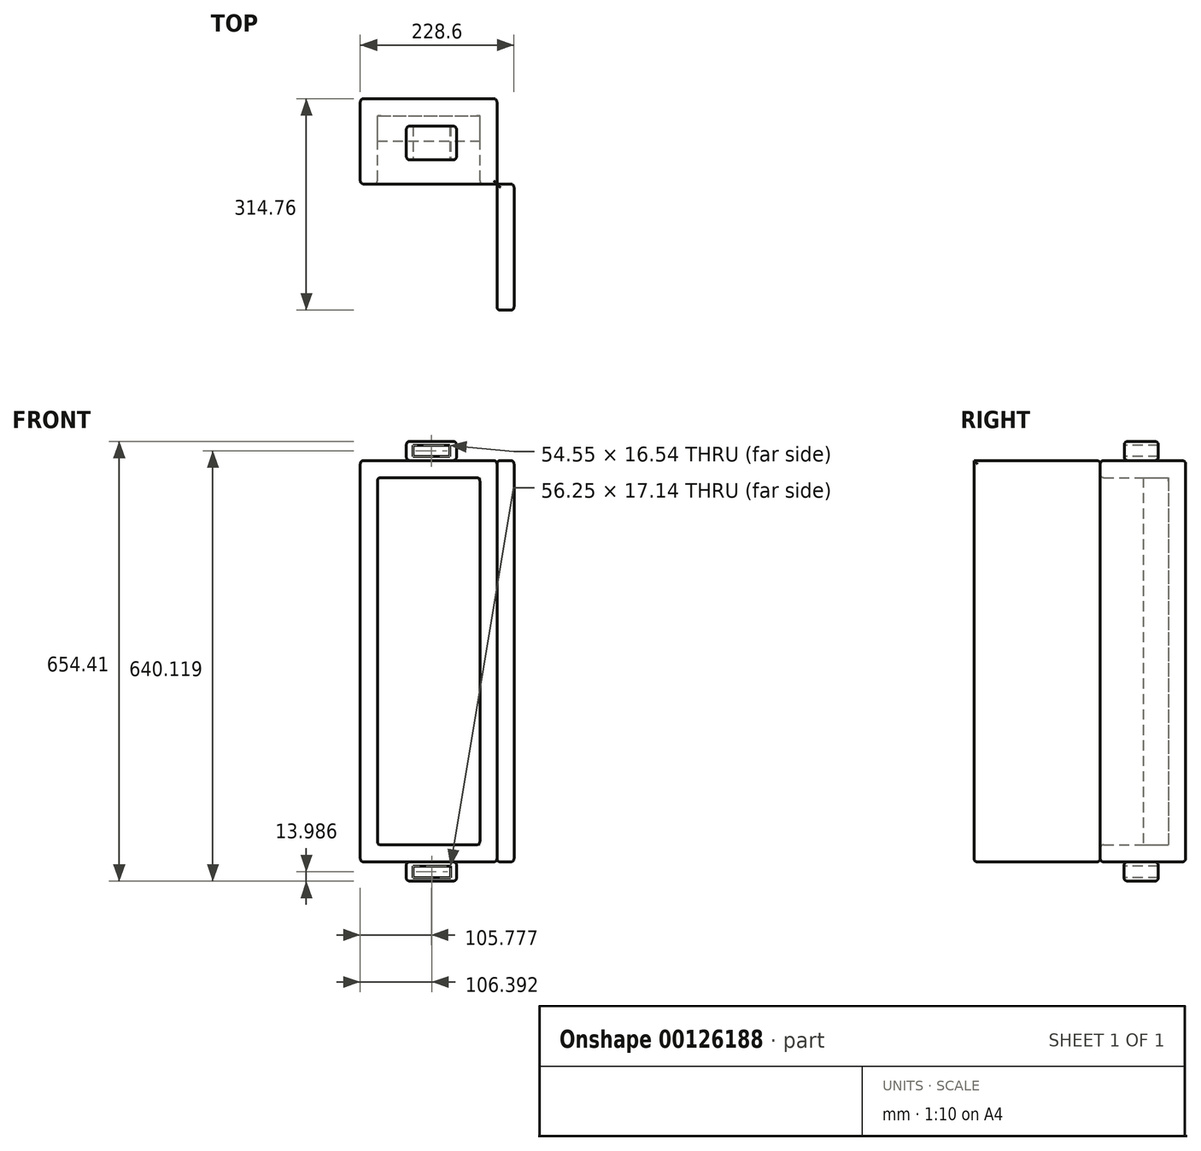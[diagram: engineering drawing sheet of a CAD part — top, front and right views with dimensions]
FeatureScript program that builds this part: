
annotation { "Feature Type Name" : "Feature", "Feature Type Description" : "" }
export const myFeature = defineFeature(function(context is Context, id is Id, definition is map)
    precondition{}
    {
        {
            var Q0;
            Q0=qCreatedBy(makeId("Front.planeOp"),FACE);
            var sketch = newSketch(context, id + "F0", { "sketchPlane" : qUnion([Q0])});
            skLineSegment(sketch, "E0.bottom", {"start": v(-31.04, 96) * mm, "end": v(172.16, 96) * mm});
            skLineSegment(sketch, "E0.top", {"start": v(-31.04, -501.25) * mm, "end": v(172.16, -501.25) * mm});
            skLineSegment(sketch, "E0.left", {"start": v(-31.04, 96) * mm, "end": v(-31.04, -501.25) * mm});
            skLineSegment(sketch, "E0.right", {"start": v(172.16, 96) * mm, "end": v(172.16, -501.25) * mm});
            skSolve(sketch);
        }
        {
            var Q0;
            Q0 = qSketchRegion(id + "F0", true);
            extrude(context, id + "F1", {"entities" : qUnion([Q0]), "depth" : 127 * mm});
        }
        {
            var Q0;
            Q0=makeQuery(id+"F1.opExtrude","CAP_FACE",FACE,{"disambiguationData":[OSD([sQuery(id+"F0.wireOp",EDGE,"E0.bottom"),sQuery(id+"F0.wireOp",EDGE,"E0.top"),sQuery(id+"F0.wireOp",EDGE,"E0.left"),sQuery(id+"F0.wireOp",EDGE,"E0.right")])],"isStart":false});
            shell(context, id + "F2", {"entities" : qUnion([Q0]), "thickness" : 25.4 * mm});
        }
        {
            var Q0;
            Q0=makeQuery(id+"F2.opShell","OFFSET_FACE",FACE,{"disambiguationData":[OSD([sQuery(id+"F0.wireOp",EDGE,"E0.bottom"),sQuery(id+"F0.wireOp",EDGE,"E0.top"),sQuery(id+"F0.wireOp",EDGE,"E0.left"),sQuery(id+"F0.wireOp",EDGE,"E0.right")])]});
            var sketch = newSketch(context, id + "F3", { "sketchPlane" : qUnion([Q0])});
            skLineSegment(sketch, "E1", {"start": v(-5.64, 70.6) * mm, "end": v(146.76, 70.6) * mm});
            skLineSegment(sketch, "E2", {"start": v(146.76, 70.6) * mm, "end": v(146.76, -475.85) * mm});
            skLineSegment(sketch, "E3", {"start": v(146.76, -475.85) * mm, "end": v(-5.64, -475.85) * mm});
            skLineSegment(sketch, "E4", {"start": v(-5.64, -475.85) * mm, "end": v(-5.64, 70.6) * mm});
            skSolve(sketch);
        }
        {
            var Q0;
            Q0 = qSketchRegion(id + "F3", true);
            extrude(context, id + "F4", {"entities" : qUnion([Q0]), "depth" : 37.53 * mm});
        }
        {
            var Q0;
            Q0=makeQuery(id+"F1.opExtrude","SWEPT_FACE",FACE,{"disambiguationData":[OSD([sQuery(id+"F0.wireOp",EDGE,"E0.right")])]});
            var sketch = newSketch(context, id + "F5", { "sketchPlane" : qUnion([Q0])});
            skLineSegment(sketch, "E5", {"start": v(-127, -501.25) * mm, "end": v(-314.76, -501.25) * mm});
            skLineSegment(sketch, "E6", {"start": v(-314.76, -501.25) * mm, "end": v(-314.76, 96) * mm});
            skLineSegment(sketch, "E7", {"start": v(-314.76, 96) * mm, "end": v(-127, 96) * mm});
            skLineSegment(sketch, "E8", {"start": v(-127, 96) * mm, "end": v(-127, -501.25) * mm});
            skSolve(sketch);
        }
        {
            var Q0;
            Q0 = qSketchRegion(id + "F5", true);
            extrude(context, id + "F6", {"entities" : qUnion([Q0]), "depth" : 25.4 * mm});
        }
        {
            var Q0;
            Q0=makeQuery(id+"F1.opExtrude","SWEPT_FACE",FACE,{"disambiguationData":[OSD([sQuery(id+"F0.wireOp",EDGE,"E0.top")])]});
            var sketch = newSketch(context, id + "F7", { "sketchPlane" : qUnion([Q0])});
            skLineSegment(sketch, "E9.bottom", {"start": v(37.26, 91.6) * mm, "end": v(112.22, 91.6) * mm});
            skLineSegment(sketch, "E9.top", {"start": v(37.26, 40.74) * mm, "end": v(112.22, 40.74) * mm});
            skLineSegment(sketch, "E9.left", {"start": v(37.26, 91.6) * mm, "end": v(37.26, 40.74) * mm});
            skLineSegment(sketch, "E9.right", {"start": v(112.22, 91.6) * mm, "end": v(112.22, 40.74) * mm});
            skSolve(sketch);
        }
        {
            var Q0;
            Q0 = qSketchRegion(id + "F7", true);
            extrude(context, id + "F8", {"entities" : qUnion([Q0]), "depth" : 28.58 * mm});
        }
        {
            var Q0;
            Q0=makeQuery(id+"F8.opExtrude","SWEPT_FACE",FACE,{"disambiguationData":[OSD([sQuery(id+"F7.wireOp",EDGE,"E9.bottom")])]});
            var sketch = newSketch(context, id + "F9", { "sketchPlane" : qUnion([Q0])});
            skLineSegment(sketch, "E10.bottom", {"start": v(47.23, -507.27) * mm, "end": v(103.48, -507.27) * mm});
            skLineSegment(sketch, "E10.top", {"start": v(47.23, -524.42) * mm, "end": v(103.48, -524.42) * mm});
            skLineSegment(sketch, "E10.left", {"start": v(47.23, -507.27) * mm, "end": v(47.23, -524.42) * mm});
            skLineSegment(sketch, "E10.right", {"start": v(103.48, -507.27) * mm, "end": v(103.48, -524.42) * mm});
            skSolve(sketch);
        }
        {
            var Q0;
            Q0 = qSketchRegion(id + "F9", true);
            extrude(context, id + "F10", {"entities" : qUnion([Q0]), "operationType" : NewBodyOperationType.REMOVE, "oppositeDirection" : true, "depth" : 76.2 * mm});
        }
        {
            var Q0;
            Q0=makeQuery(id+"F1.opExtrude","SWEPT_FACE",FACE,{"disambiguationData":[OSD([sQuery(id+"F0.wireOp",EDGE,"E0.bottom")])]});
            var sketch = newSketch(context, id + "F11", { "sketchPlane" : qUnion([Q0])});
            skLineSegment(sketch, "E11.bottom", {"start": v(37.48, -40.74) * mm, "end": v(112, -40.74) * mm});
            skLineSegment(sketch, "E11.top", {"start": v(37.48, -91.16) * mm, "end": v(112, -91.16) * mm});
            skLineSegment(sketch, "E11.left", {"start": v(37.48, -40.74) * mm, "end": v(37.48, -91.16) * mm});
            skLineSegment(sketch, "E11.right", {"start": v(112, -40.74) * mm, "end": v(112, -91.16) * mm});
            skSolve(sketch);
        }
        {
            var Q0;
            Q0 = qSketchRegion(id + "F11", true);
            extrude(context, id + "F12", {"entities" : qUnion([Q0]), "depth" : 28.57 * mm});
        }
        {
            var Q0;
            Q0=makeQuery(id+"F12.opExtrude","SWEPT_FACE",FACE,{"disambiguationData":[OSD([sQuery(id+"F11.wireOp",EDGE,"E11.top")])]});
            var sketch = newSketch(context, id + "F13", { "sketchPlane" : qUnion([Q0])});
            skLineSegment(sketch, "E12.bottom", {"start": v(47.46, 118.56) * mm, "end": v(102.01, 118.56) * mm});
            skLineSegment(sketch, "E12.top", {"start": v(47.46, 102.02) * mm, "end": v(102.01, 102.02) * mm});
            skLineSegment(sketch, "E12.left", {"start": v(47.46, 118.56) * mm, "end": v(47.46, 102.02) * mm});
            skLineSegment(sketch, "E12.right", {"start": v(102.01, 118.56) * mm, "end": v(102.01, 102.02) * mm});
            skSolve(sketch);
        }
        {
            var Q0;
            Q0 = qSketchRegion(id + "F13", true);
            extrude(context, id + "F14", {"entities" : qUnion([Q0]), "operationType" : NewBodyOperationType.REMOVE, "oppositeDirection" : true, "depth" : 76.2 * mm});
        }
        {
            var Q0;
            Q0=makeQuery(id+"F8.opExtrude","CAP_EDGE",EDGE,{"disambiguationData":[OSD([sQuery(id+"F7.wireOp",EDGE,"E9.left")])],"isStart":true});
            var Q1;
            Q1=makeQuery(id+"F8.opExtrude","CAP_EDGE",EDGE,{"disambiguationData":[OSD([sQuery(id+"F7.wireOp",EDGE,"E9.bottom")])],"isStart":true});
            var Q2;
            Q2=makeQuery(id+"F8.opExtrude","CAP_EDGE",EDGE,{"disambiguationData":[OSD([sQuery(id+"F7.wireOp",EDGE,"E9.right")])],"isStart":true});
            var Q3;
            Q3=makeQuery(id+"F8.opExtrude","CAP_EDGE",EDGE,{"disambiguationData":[OSD([sQuery(id+"F7.wireOp",EDGE,"E9.top")])],"isStart":true});
            var Q4;
            Q4=makeQuery(id+"F8.opExtrude","SWEPT_EDGE",EDGE,{"disambiguationData":[OSD([sQuery(id+"F7.wireOp",EDGE,"E9.top"),sQuery(id+"F7.wireOp",EDGE,"E9.right")])]});
            var Q5;
            Q5=makeQuery(id+"F8.opExtrude","SWEPT_EDGE",EDGE,{"disambiguationData":[OSD([sQuery(id+"F7.wireOp",EDGE,"E9.bottom"),sQuery(id+"F7.wireOp",EDGE,"E9.right")])]});
            var Q6;
            Q6=makeQuery(id+"F8.opExtrude","CAP_EDGE",EDGE,{"disambiguationData":[OSD([sQuery(id+"F7.wireOp",EDGE,"E9.right")])],"isStart":false});
            var Q7;
            Q7=makeQuery(id+"F8.opExtrude","CAP_EDGE",EDGE,{"disambiguationData":[OSD([sQuery(id+"F7.wireOp",EDGE,"E9.bottom")])],"isStart":false});
            var Q8;
            Q8=makeQuery(id+"F8.opExtrude","CAP_EDGE",EDGE,{"disambiguationData":[OSD([sQuery(id+"F7.wireOp",EDGE,"E9.left")])],"isStart":false});
            var Q9;
            Q9=makeQuery(id+"F8.opExtrude","SWEPT_EDGE",EDGE,{"disambiguationData":[OSD([sQuery(id+"F7.wireOp",EDGE,"E9.bottom"),sQuery(id+"F7.wireOp",EDGE,"E9.left")])]});
            var Q10;
            Q10=makeQuery(id+"F8.opExtrude","CAP_EDGE",EDGE,{"disambiguationData":[OSD([sQuery(id+"F7.wireOp",EDGE,"E9.top")])],"isStart":false});
            var Q11;
            Q11=makeQuery(id+"F8.opExtrude","SWEPT_EDGE",EDGE,{"disambiguationData":[OSD([sQuery(id+"F7.wireOp",EDGE,"E9.top"),sQuery(id+"F7.wireOp",EDGE,"E9.left")])]});
            fillet(context, id + "F15", {"entities" : qUnion([Q0, Q1, Q2, Q3, Q4, Q5, Q6, Q7, Q8, Q9, Q10, Q11]), "radius" : 5.08 * mm, "tangentPropagation" : true, "allowEdgeOverflow" : false});
        }
        {
            var Q0;
            Q0=makeQuery(id+"F12.opExtrude","SWEPT_EDGE",EDGE,{"disambiguationData":[OSD([sQuery(id+"F11.wireOp",EDGE,"E11.top"),sQuery(id+"F11.wireOp",EDGE,"E11.right")])]});
            var Q1;
            Q1=makeQuery(id+"F12.opExtrude","CAP_EDGE",EDGE,{"disambiguationData":[OSD([sQuery(id+"F11.wireOp",EDGE,"E11.top")])],"isStart":true});
            var Q2;
            Q2=makeQuery(id+"F12.opExtrude","CAP_EDGE",EDGE,{"disambiguationData":[OSD([sQuery(id+"F11.wireOp",EDGE,"E11.top")])],"isStart":false});
            var Q3;
            Q3=makeQuery(id+"F12.opExtrude","SWEPT_EDGE",EDGE,{"disambiguationData":[OSD([sQuery(id+"F11.wireOp",EDGE,"E11.top"),sQuery(id+"F11.wireOp",EDGE,"E11.left")])]});
            var Q4;
            Q4=makeQuery(id+"F12.opExtrude","CAP_EDGE",EDGE,{"disambiguationData":[OSD([sQuery(id+"F11.wireOp",EDGE,"E11.left")])],"isStart":true});
            var Q5;
            Q5=makeQuery(id+"F12.opExtrude","CAP_EDGE",EDGE,{"disambiguationData":[OSD([sQuery(id+"F11.wireOp",EDGE,"E11.left")])],"isStart":false});
            var Q6;
            Q6=makeQuery(id+"F12.opExtrude","CAP_EDGE",EDGE,{"disambiguationData":[OSD([sQuery(id+"F11.wireOp",EDGE,"E11.right")])],"isStart":false});
            var Q7;
            Q7=makeQuery(id+"F12.opExtrude","CAP_EDGE",EDGE,{"disambiguationData":[OSD([sQuery(id+"F11.wireOp",EDGE,"E11.bottom")])],"isStart":false});
            var Q8;
            Q8=makeQuery(id+"F12.opExtrude","CAP_EDGE",EDGE,{"disambiguationData":[OSD([sQuery(id+"F11.wireOp",EDGE,"E11.right")])],"isStart":true});
            var Q9;
            Q9=makeQuery(id+"F12.opExtrude","SWEPT_EDGE",EDGE,{"disambiguationData":[OSD([sQuery(id+"F11.wireOp",EDGE,"E11.bottom"),sQuery(id+"F11.wireOp",EDGE,"E11.right")])]});
            var Q10;
            Q10=makeQuery(id+"F12.opExtrude","SWEPT_EDGE",EDGE,{"disambiguationData":[OSD([sQuery(id+"F11.wireOp",EDGE,"E11.bottom"),sQuery(id+"F11.wireOp",EDGE,"E11.left")])]});
            var Q11;
            Q11=makeQuery(id+"F12.opExtrude","CAP_EDGE",EDGE,{"disambiguationData":[OSD([sQuery(id+"F11.wireOp",EDGE,"E11.bottom")])],"isStart":true});
            fillet(context, id + "F16", {"entities" : qUnion([Q0, Q1, Q2, Q3, Q4, Q5, Q6, Q7, Q8, Q9, Q10, Q11]), "radius" : 5.08 * mm, "tangentPropagation" : true, "allowEdgeOverflow" : false});
        }
        {
            var Q0;
            Q0=makeQuery(id+"F1.opExtrude","SWEPT_EDGE",EDGE,{"disambiguationData":[OSD([sQuery(id+"F0.wireOp",EDGE,"E0.bottom"),sQuery(id+"F0.wireOp",EDGE,"E0.left")])]});
            var Q1;
            Q1=makeQuery(id+"F1.opExtrude","SWEPT_EDGE",EDGE,{"disambiguationData":[OSD([sQuery(id+"F0.wireOp",EDGE,"E0.bottom"),sQuery(id+"F0.wireOp",EDGE,"E0.right")])]});
            var Q2;
            Q2=makeQuery(id+"F1.opExtrude","CAP_EDGE",EDGE,{"disambiguationData":[OSD([sQuery(id+"F0.wireOp",EDGE,"E0.bottom")])],"isStart":false});
            var Q3;
            Q3=makeQuery(id+"F1.opExtrude","CAP_EDGE",EDGE,{"disambiguationData":[OSD([sQuery(id+"F0.wireOp",EDGE,"E0.bottom")])],"isStart":true});
            var Q4;
            Q4=makeQuery(id+"F1.opExtrude","CAP_EDGE",EDGE,{"disambiguationData":[OSD([sQuery(id+"F0.wireOp",EDGE,"E0.left")])],"isStart":true});
            var Q5;
            Q5=makeQuery(id+"F1.opExtrude","CAP_EDGE",EDGE,{"disambiguationData":[OSD([sQuery(id+"F0.wireOp",EDGE,"E0.left")])],"isStart":false});
            var Q6;
            Q6=makeQuery(id+"F1.opExtrude","CAP_EDGE",EDGE,{"disambiguationData":[OSD([sQuery(id+"F0.wireOp",EDGE,"E0.top")])],"isStart":true});
            var Q7;
            Q7=makeQuery(id+"F1.opExtrude","SWEPT_EDGE",EDGE,{"disambiguationData":[OSD([sQuery(id+"F0.wireOp",EDGE,"E0.top"),sQuery(id+"F0.wireOp",EDGE,"E0.left")])]});
            var Q8;
            Q8=makeQuery(id+"F1.opExtrude","SWEPT_EDGE",EDGE,{"disambiguationData":[OSD([sQuery(id+"F0.wireOp",EDGE,"E0.top"),sQuery(id+"F0.wireOp",EDGE,"E0.right")])]});
            var Q9;
            Q9=makeQuery(id+"F1.opExtrude","CAP_EDGE",EDGE,{"disambiguationData":[OSD([sQuery(id+"F0.wireOp",EDGE,"E0.top")])],"isStart":false});
            var Q10;
            Q10=makeQuery(id+"F1.opExtrude","CAP_EDGE",EDGE,{"disambiguationData":[OSD([sQuery(id+"F0.wireOp",EDGE,"E0.right")])],"isStart":true});
            var Q11;
            Q11=makeQuery(id+"F6.opExtrude","CAP_EDGE",EDGE,{"disambiguationData":[OSD([sQuery(id+"F5.wireOp",EDGE,"E5")])],"isStart":true});
            var Q12;
            Q12=makeQuery(id+"F6.opExtrude","CAP_EDGE",EDGE,{"disambiguationData":[OSD([sQuery(id+"F5.wireOp",EDGE,"E7")])],"isStart":true});
            var Q13;
            Q13=makeQuery(id+"F6.opExtrude","CAP_EDGE",EDGE,{"disambiguationData":[OSD([sQuery(id+"F5.wireOp",EDGE,"E6")])],"isStart":true});
            var Q14;
            Q14=makeQuery(id+"F6.opExtrude","SWEPT_EDGE",EDGE,{"disambiguationData":[OSD([sQuery(id+"F0.wireOp",EDGE,"E0.bottom"),sQuery(id+"F0.wireOp",EDGE,"E0.right"),sQuery(id+"F5.wireOp",EDGE,"E7"),sQuery(id+"F5.wireOp",EDGE,"E8")])]});
            var Q15;
            Q15=makeQuery(id+"F6.opExtrude","CAP_EDGE",EDGE,{"disambiguationData":[OSD([sQuery(id+"F5.wireOp",EDGE,"E8")])],"isStart":false});
            var Q16;
            Q16=makeQuery(id+"F6.opExtrude","CAP_EDGE",EDGE,{"disambiguationData":[OSD([sQuery(id+"F5.wireOp",EDGE,"E7")])],"isStart":false});
            var Q17;
            Q17=makeQuery(id+"F6.opExtrude","CAP_EDGE",EDGE,{"disambiguationData":[OSD([sQuery(id+"F5.wireOp",EDGE,"E6")])],"isStart":false});
            var Q18;
            Q18=makeQuery(id+"F6.opExtrude","CAP_EDGE",EDGE,{"disambiguationData":[OSD([sQuery(id+"F5.wireOp",EDGE,"E5")])],"isStart":false});
            var Q19;
            Q19=makeQuery(id+"F6.opExtrude","SWEPT_EDGE",EDGE,{"disambiguationData":[OSD([sQuery(id+"F5.wireOp",EDGE,"E5"),sQuery(id+"F5.wireOp",EDGE,"E6")])]});
            var Q20;
            Q20=makeQuery(id+"F6.opExtrude","SWEPT_EDGE",EDGE,{"disambiguationData":[OSD([sQuery(id+"F0.wireOp",EDGE,"E0.top"),sQuery(id+"F0.wireOp",EDGE,"E0.right"),sQuery(id+"F5.wireOp",EDGE,"E5"),sQuery(id+"F5.wireOp",EDGE,"E8")])]});
            fillet(context, id + "F17", {"entities" : qUnion([Q0, Q1, Q2, Q3, Q4, Q5, Q6, Q7, Q8, Q9, Q10, Q11, Q12, Q13, Q14, Q15, Q16, Q17, Q18, Q19, Q20]), "radius" : 5.08 * mm, "tangentPropagation" : true, "allowEdgeOverflow" : false});
        }
        {
            var Q0;
            {var subQ0=sQuery(id+"F0.wireOp",EDGE,"E0.bottom");Q0=makeQuery(id+"F2.opShell","OFFSET_EDGE",EDGE,{"disambiguationData":[OSD([subQ0]),TDD([makeQuery(id+"F1.opExtrude","CAP_EDGE",EDGE,{"disambiguationData":[OSD([subQ0])],"isStart":false})])]});}
            var Q1;
            {var subQ0=sQuery(id+"F0.wireOp",EDGE,"E0.right");Q1=makeQuery(id+"F2.opShell","OFFSET_EDGE",EDGE,{"disambiguationData":[OSD([subQ0]),TDD([makeQuery(id+"F1.opExtrude","CAP_EDGE",EDGE,{"disambiguationData":[OSD([subQ0])],"isStart":false})])]});}
            var Q2;
            {var subQ0=sQuery(id+"F0.wireOp",EDGE,"E0.left");Q2=makeQuery(id+"F2.opShell","OFFSET_EDGE",EDGE,{"disambiguationData":[OSD([subQ0]),TDD([makeQuery(id+"F1.opExtrude","CAP_EDGE",EDGE,{"disambiguationData":[OSD([subQ0])],"isStart":false})])]});}
            var Q3;
            {var subQ0=sQuery(id+"F0.wireOp",EDGE,"E0.top");Q3=makeQuery(id+"F2.opShell","OFFSET_EDGE",EDGE,{"disambiguationData":[OSD([subQ0]),TDD([makeQuery(id+"F1.opExtrude","CAP_EDGE",EDGE,{"disambiguationData":[OSD([subQ0])],"isStart":false})])]});}
            var Q4;
            Q4=makeQuery(id+"F2.opShell","OFFSET_EDGE",EDGE,{"disambiguationData":[OSD([sQuery(id+"F0.wireOp",EDGE,"E0.top"),sQuery(id+"F0.wireOp",EDGE,"E0.right")])]});
            var Q5;
            Q5=makeQuery(id+"F2.opShell","OFFSET_EDGE",EDGE,{"disambiguationData":[OSD([sQuery(id+"F0.wireOp",EDGE,"E0.top"),sQuery(id+"F0.wireOp",EDGE,"E0.left")])]});
            var Q6;
            Q6=makeQuery(id+"F2.opShell","OFFSET_EDGE",EDGE,{"disambiguationData":[OSD([sQuery(id+"F0.wireOp",EDGE,"E0.bottom"),sQuery(id+"F0.wireOp",EDGE,"E0.left")])]});
            var Q7;
            Q7=makeQuery(id+"F2.opShell","OFFSET_EDGE",EDGE,{"disambiguationData":[OSD([sQuery(id+"F0.wireOp",EDGE,"E0.bottom"),sQuery(id+"F0.wireOp",EDGE,"E0.right")])]});
            fillet(context, id + "F18", {"entities" : qUnion([Q0, Q1, Q2, Q3, Q4, Q5, Q6, Q7]), "radius" : 5.08 * mm, "tangentPropagation" : true, "allowEdgeOverflow" : false});
        }
    });
